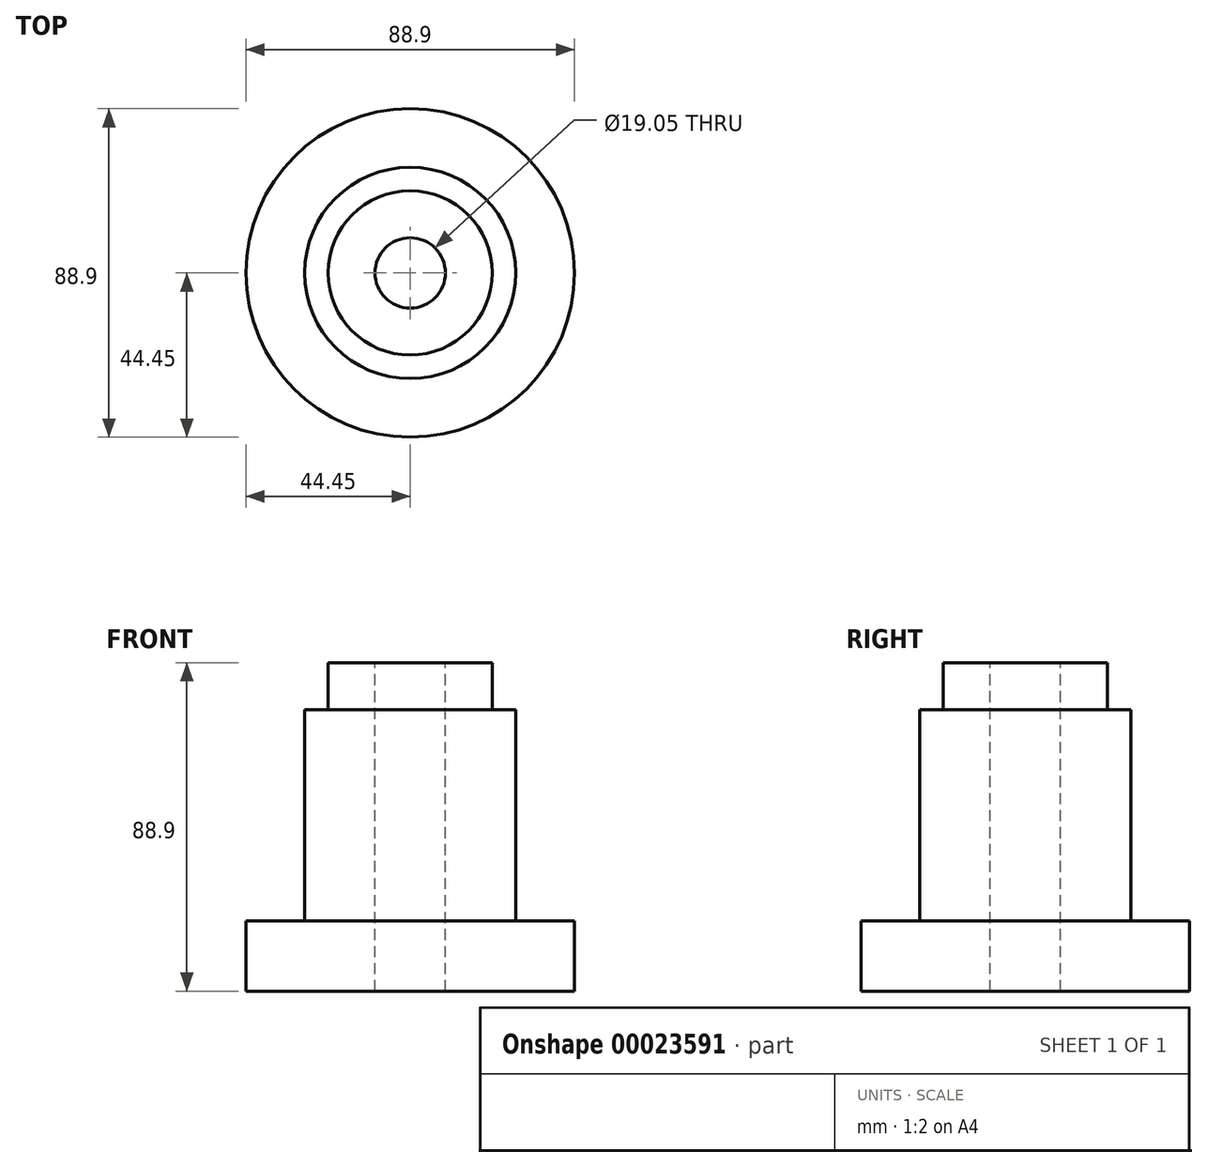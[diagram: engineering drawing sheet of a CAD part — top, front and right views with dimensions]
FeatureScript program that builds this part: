
annotation { "Feature Type Name" : "Feature", "Feature Type Description" : "" }
export const myFeature = defineFeature(function(context is Context, id is Id, definition is map)
    precondition{}
    {
        {
            var Q0;
            Q0=qCreatedBy(makeId("Front.planeOp"),FACE);
            var sketch = newSketch(context, id + "F0", { "sketchPlane" : qUnion([Q0])});
            skLineSegment(sketch, "E0", {"start": v(0, 48.5) * mm, "end": v(0, -77.92) * mm, "construction": true});
            skLineSegment(sketch, "E1", {"start": v(-9.52, 48.5) * mm, "end": v(-9.52, 35.8) * mm});
            skLineSegment(sketch, "E2.bottom", {"start": v(-9.52, 35.8) * mm, "end": v(-22.23, 35.8) * mm});
            skLineSegment(sketch, "E2.top", {"start": v(-9.53, 48.5) * mm, "end": v(-22.23, 48.5) * mm});
            skLineSegment(sketch, "E2.left", {"start": v(-9.52, 35.8) * mm, "end": v(-9.53, 48.5) * mm});
            skLineSegment(sketch, "E2.right", {"start": v(-22.23, 35.8) * mm, "end": v(-22.23, 48.5) * mm});
            skLineSegment(sketch, "E3.bottom", {"start": v(-9.52, 35.8) * mm, "end": v(-28.58, 35.8) * mm});
            skLineSegment(sketch, "E3.top", {"start": v(-9.52, -21.35) * mm, "end": v(-28.57, -21.35) * mm});
            skLineSegment(sketch, "E3.left", {"start": v(-9.53, 35.8) * mm, "end": v(-9.52, -21.35) * mm});
            skLineSegment(sketch, "E3.right", {"start": v(-28.58, 35.8) * mm, "end": v(-28.57, -21.35) * mm});
            skLineSegment(sketch, "E4.bottom", {"start": v(-9.52, -21.35) * mm, "end": v(-44.45, -21.35) * mm});
            skLineSegment(sketch, "E4.top", {"start": v(-9.52, -40.4) * mm, "end": v(-44.45, -40.4) * mm});
            skLineSegment(sketch, "E4.left", {"start": v(-9.52, -21.35) * mm, "end": v(-9.52, -40.4) * mm});
            skLineSegment(sketch, "E4.right", {"start": v(-44.45, -21.35) * mm, "end": v(-44.45, -40.4) * mm});
            skLineSegment(sketch, "E5", {"start": v(-9.53, 48.5) * mm, "end": v(-9.52, -40.4) * mm});
            skSolve(sketch);
        }
        {
            var Q0;
            Q0 = qSketchRegion(id + "F0", true);
            var Q1;
            Q1=sQuery(id+"F0.wireOp",EDGE,"E0");
            revolve(context, id + "F1", {"entities" : qUnion([Q0]), "axis" : qUnion([Q1]), "revolveType" : RevolveType.FULL});
        }
    });
